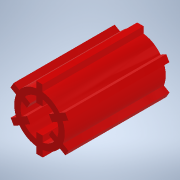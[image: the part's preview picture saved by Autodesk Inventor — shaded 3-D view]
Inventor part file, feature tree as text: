
AUTODESK INVENTOR PART (.ipt)
format: ipt  version: 2021 (Build 250183000, 183)  size: 166,912 bytes
history: native  units: in
note: dims shown in document units (in); Inventor stores cm internally (conversion verified against a paired STEP export)
features: extrude x1, sketch x1
ambient origin geometry x8: Origin, YZ Plane, XZ Plane, XY Plane, X Axis, Y Axis, Z Axis, Center Point
bodies: Body1 (feature_tree)
feature tree (2):
  extrude  "Extrusion4"  Depth=0.125in
  sketch  "Sketch1"  dims[d14=2.3622in d16=360.0deg d20=0.125in d21=0.125in d22=2.3622in d24=360.0deg d27=0.0in]
